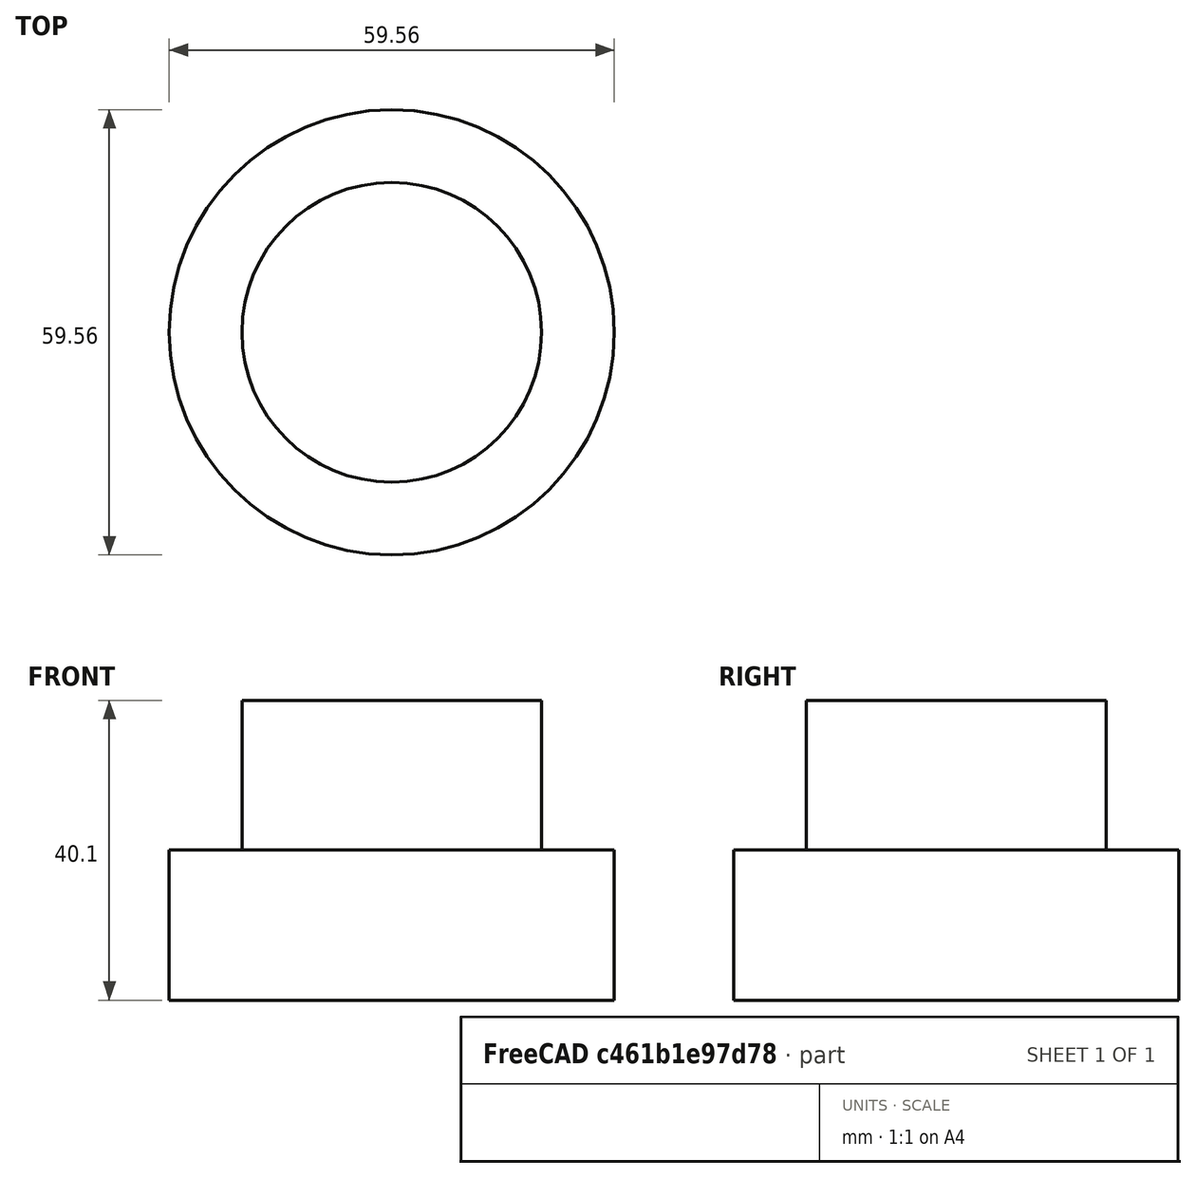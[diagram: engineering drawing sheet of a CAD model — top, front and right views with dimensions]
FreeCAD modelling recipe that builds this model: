
FCSTD DOCUMENT  (FreeCAD 0.20R29410 (Git))
Label: Cylindre
License: All rights reserved
LicenseURL: http://en.wikipedia.org/wiki/All_rights_reserved
objects: Sketcher::SketchObject×1, PartDesign::Revolution×1, PartDesign::Body×1
note: 4 computed .brp shape members not serialized (recipe doc carries the construction recipe); baked Part::Feature solids carry a one-line shape summary decoded from their .brp

FEATURE [Sketcher::SketchObject] Sketch
  FullyConstrained = false
  MapMode = 5
  Placement = pos=(0,0,0) rot=(1,0,0;1.5708rad)
  Support = -> [XZ_Plane]
  sketch-geometry (6):
    g0: LineSegment StartX=0 StartY=0 StartZ=0 EndX=-29.7819 EndY=0 EndZ=0
    g1: LineSegment StartX=-29.7819 StartY=0 StartZ=0 EndX=-29.7819 EndY=20.1342 EndZ=0
    g2: LineSegment StartX=-29.7819 StartY=20.1342 StartZ=0 EndX=-20.0503 EndY=20.1342 EndZ=0
    g3: LineSegment StartX=-20.0503 StartY=20.1342 StartZ=0 EndX=-20.0503 EndY=40.1007 EndZ=0
    g4: LineSegment StartX=-20.0503 StartY=40.1007 StartZ=0 EndX=0 EndY=40.1007 EndZ=0
    g5: LineSegment StartX=0 StartY=40.1007 StartZ=0 EndX=0 EndY=0 EndZ=0
  constraints (13):
    c: Coincident(g-1,g0)
    c: Horizontal(g0)
    c: Coincident(g0,g1)
    c: Vertical(g1)
    c: Coincident(g1,g2)
    c: Horizontal(g2)
    c: Coincident(g2,g3)
    c: Vertical(g3)
    c: Coincident(g3,g4)
    c: PointOnObject(g4,g-2)
    c: Horizontal(g4)
    c: Coincident(g4,g5)
    c: Coincident(g5,g0)
FEATURE [PartDesign::Revolution] Revolution
  Angle = 360
  Axis = (0,2e-16,1)
  Base = (0,0,0)
  Placement = pos=(0,0,0) rot=(1,0,0;1.5708rad)
  Profile = -> Sketch
  ReferenceAxis = -> Sketch [V_Axis]
FEATURE [PartDesign::Body] Body
  Group = -> [Sketch,Revolution]
  Origin = -> Origin
  Tip = -> Revolution
